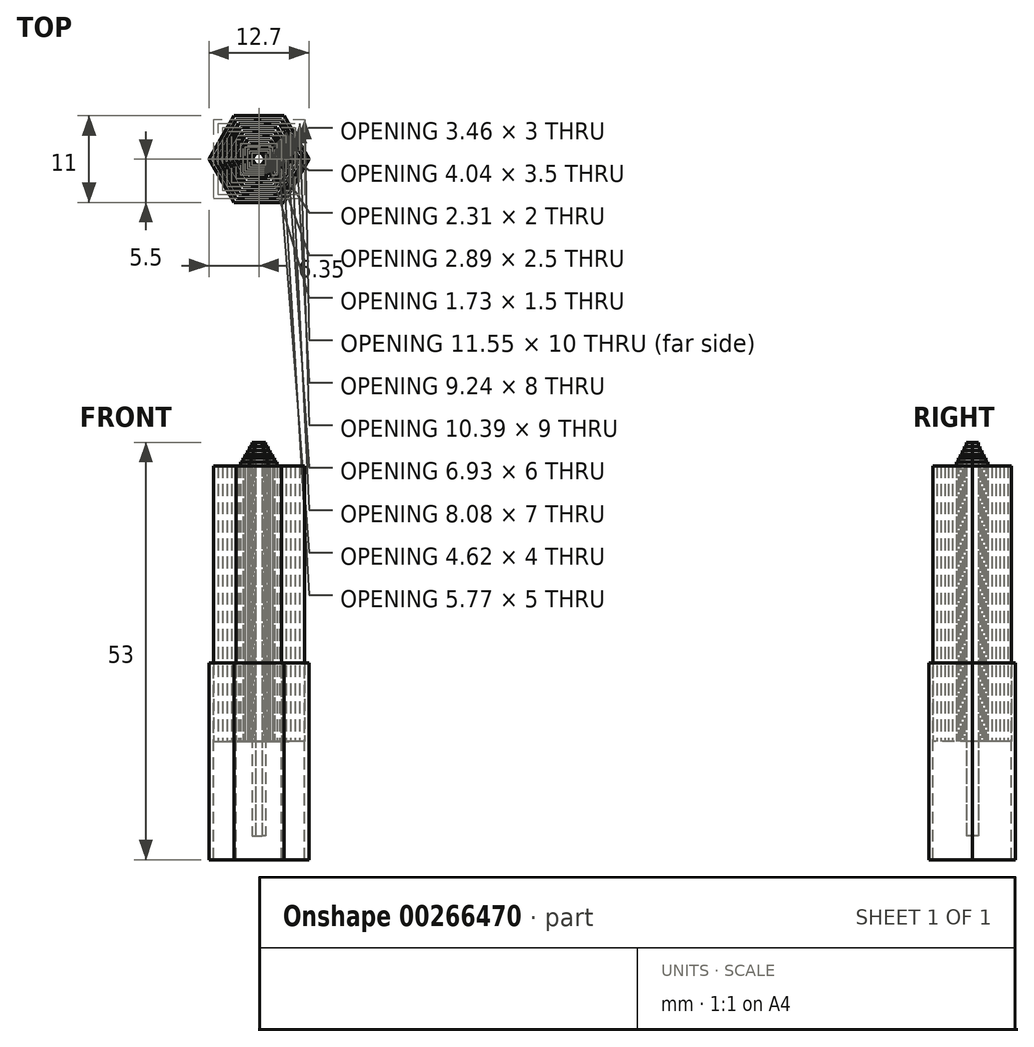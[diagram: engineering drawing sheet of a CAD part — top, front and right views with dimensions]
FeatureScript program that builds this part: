
annotation { "Feature Type Name" : "Feature", "Feature Type Description" : "" }
export const myFeature = defineFeature(function(context is Context, id is Id, definition is map)
    precondition{}
    {
        {
            var Q0;
            Q0=qCreatedBy(makeId("Top.planeOp"),FACE);
            var sketch = newSketch(context, id + "F0", { "sketchPlane" : qUnion([Q0])});
            skCircle(sketch, "E0.cCircle", {"center": v(0, 0) * mm, "radius": 0.87 * mm, "construction": true});
            skLineSegment(sketch, "E0.0", {"start": v(0.87, 0) * mm, "end": v(0.43, -0.75) * mm});
            skLineSegment(sketch, "E0.1", {"start": v(0.43, -0.75) * mm, "end": v(-0.43, -0.75) * mm});
            skLineSegment(sketch, "E0.2", {"start": v(-0.43, -0.75) * mm, "end": v(-0.87, 0) * mm});
            skLineSegment(sketch, "E0.3", {"start": v(-0.87, 0) * mm, "end": v(-0.43, 0.75) * mm});
            skLineSegment(sketch, "E0.4", {"start": v(-0.43, 0.75) * mm, "end": v(0.43, 0.75) * mm});
            skLineSegment(sketch, "E0.5", {"start": v(0.43, 0.75) * mm, "end": v(0.87, 0) * mm});
            skCircle(sketch, "E1.cCircle", {"center": v(0, 0) * mm, "radius": 1.15 * mm, "construction": true});
            skLineSegment(sketch, "E1.0", {"start": v(1.15, 0) * mm, "end": v(0.58, -1) * mm});
            skLineSegment(sketch, "E1.1", {"start": v(0.58, -1) * mm, "end": v(-0.58, -1) * mm});
            skLineSegment(sketch, "E1.2", {"start": v(-0.58, -1) * mm, "end": v(-1.15, 0) * mm});
            skLineSegment(sketch, "E1.3", {"start": v(-1.15, 0) * mm, "end": v(-0.58, 1) * mm});
            skLineSegment(sketch, "E1.4", {"start": v(-0.58, 1) * mm, "end": v(0.58, 1) * mm});
            skLineSegment(sketch, "E1.5", {"start": v(0.58, 1) * mm, "end": v(1.15, 0) * mm});
            skCircle(sketch, "E2.cCircle", {"center": v(0, 0) * mm, "radius": 1.44 * mm, "construction": true});
            skLineSegment(sketch, "E2.0", {"start": v(1.44, 0) * mm, "end": v(0.72, -1.25) * mm});
            skLineSegment(sketch, "E2.1", {"start": v(0.72, -1.25) * mm, "end": v(-0.72, -1.25) * mm});
            skLineSegment(sketch, "E2.2", {"start": v(-0.72, -1.25) * mm, "end": v(-1.44, 0) * mm});
            skLineSegment(sketch, "E2.3", {"start": v(-1.44, 0) * mm, "end": v(-0.72, 1.25) * mm});
            skLineSegment(sketch, "E2.4", {"start": v(-0.72, 1.25) * mm, "end": v(0.72, 1.25) * mm});
            skLineSegment(sketch, "E2.5", {"start": v(0.72, 1.25) * mm, "end": v(1.44, 0) * mm});
            skCircle(sketch, "E3.cCircle", {"center": v(0, 0) * mm, "radius": 1.73 * mm, "construction": true});
            skLineSegment(sketch, "E3.0", {"start": v(1.73, 0) * mm, "end": v(0.87, -1.5) * mm});
            skLineSegment(sketch, "E3.1", {"start": v(0.87, -1.5) * mm, "end": v(-0.87, -1.5) * mm});
            skLineSegment(sketch, "E3.2", {"start": v(-0.87, -1.5) * mm, "end": v(-1.73, 0) * mm});
            skLineSegment(sketch, "E3.3", {"start": v(-1.73, 0) * mm, "end": v(-0.87, 1.5) * mm});
            skLineSegment(sketch, "E3.4", {"start": v(-0.87, 1.5) * mm, "end": v(0.87, 1.5) * mm});
            skLineSegment(sketch, "E3.5", {"start": v(0.87, 1.5) * mm, "end": v(1.73, 0) * mm});
            skCircle(sketch, "E4.cCircle", {"center": v(0, 0) * mm, "radius": 2.02 * mm, "construction": true});
            skLineSegment(sketch, "E4.0", {"start": v(2.02, 0) * mm, "end": v(1.01, -1.75) * mm});
            skLineSegment(sketch, "E4.1", {"start": v(1.01, -1.75) * mm, "end": v(-1.01, -1.75) * mm});
            skLineSegment(sketch, "E4.2", {"start": v(-1.01, -1.75) * mm, "end": v(-2.02, 0) * mm});
            skLineSegment(sketch, "E4.3", {"start": v(-2.02, 0) * mm, "end": v(-1.01, 1.75) * mm});
            skLineSegment(sketch, "E4.4", {"start": v(-1.01, 1.75) * mm, "end": v(1.01, 1.75) * mm});
            skLineSegment(sketch, "E4.5", {"start": v(1.01, 1.75) * mm, "end": v(2.02, 0) * mm});
            skCircle(sketch, "E5.cCircle", {"center": v(0, 0) * mm, "radius": 2.3 * mm, "construction": true});
            skLineSegment(sketch, "E5.0", {"start": v(2.3, 0) * mm, "end": v(1.15, -2) * mm});
            skLineSegment(sketch, "E5.1", {"start": v(1.15, -2) * mm, "end": v(-1.15, -2) * mm});
            skLineSegment(sketch, "E5.2", {"start": v(-1.15, -2) * mm, "end": v(-2.3, 0) * mm});
            skLineSegment(sketch, "E5.3", {"start": v(-2.3, 0) * mm, "end": v(-1.15, 2) * mm});
            skLineSegment(sketch, "E5.4", {"start": v(-1.15, 2) * mm, "end": v(1.15, 2) * mm});
            skLineSegment(sketch, "E5.5", {"start": v(1.15, 2) * mm, "end": v(2.3, 0) * mm});
            skCircle(sketch, "E6.cCircle", {"center": v(0, 0) * mm, "radius": 4.04 * mm, "construction": true});
            skLineSegment(sketch, "E6.0", {"start": v(4.04, 0) * mm, "end": v(2.02, -3.5) * mm});
            skLineSegment(sketch, "E6.1", {"start": v(2.02, -3.5) * mm, "end": v(-2.02, -3.5) * mm});
            skLineSegment(sketch, "E6.2", {"start": v(-2.02, -3.5) * mm, "end": v(-4.04, 0) * mm});
            skLineSegment(sketch, "E6.3", {"start": v(-4.04, 0) * mm, "end": v(-2.02, 3.5) * mm});
            skLineSegment(sketch, "E6.4", {"start": v(-2.02, 3.5) * mm, "end": v(2.02, 3.5) * mm});
            skLineSegment(sketch, "E6.5", {"start": v(2.02, 3.5) * mm, "end": v(4.04, 0) * mm});
            skCircle(sketch, "E7.cCircle", {"center": v(0, 0) * mm, "radius": 4.62 * mm, "construction": true});
            skLineSegment(sketch, "E7.0", {"start": v(4.62, 0) * mm, "end": v(2.3, -4) * mm});
            skLineSegment(sketch, "E7.1", {"start": v(2.3, -4) * mm, "end": v(-2.3, -4) * mm});
            skLineSegment(sketch, "E7.2", {"start": v(-2.3, -4) * mm, "end": v(-4.62, 0) * mm});
            skLineSegment(sketch, "E7.3", {"start": v(-4.62, 0) * mm, "end": v(-2.3, 4) * mm});
            skLineSegment(sketch, "E7.4", {"start": v(-2.3, 4) * mm, "end": v(2.3, 4) * mm});
            skLineSegment(sketch, "E7.5", {"start": v(2.3, 4) * mm, "end": v(4.62, 0) * mm});
            skCircle(sketch, "E8.cCircle", {"center": v(0, 0) * mm, "radius": 5.2 * mm, "construction": true});
            skLineSegment(sketch, "E8.0", {"start": v(5.2, 0) * mm, "end": v(2.6, -4.5) * mm});
            skLineSegment(sketch, "E8.1", {"start": v(2.6, -4.5) * mm, "end": v(-2.6, -4.5) * mm});
            skLineSegment(sketch, "E8.2", {"start": v(-2.6, -4.5) * mm, "end": v(-5.2, 0) * mm});
            skLineSegment(sketch, "E8.3", {"start": v(-5.2, 0) * mm, "end": v(-2.6, 4.5) * mm});
            skLineSegment(sketch, "E8.4", {"start": v(-2.6, 4.5) * mm, "end": v(2.6, 4.5) * mm});
            skLineSegment(sketch, "E8.5", {"start": v(2.6, 4.5) * mm, "end": v(5.2, 0) * mm});
            skCircle(sketch, "E9.cCircle", {"center": v(0, 0) * mm, "radius": 5.77 * mm, "construction": true});
            skLineSegment(sketch, "E9.0", {"start": v(5.77, 0) * mm, "end": v(2.89, -5) * mm});
            skLineSegment(sketch, "E9.1", {"start": v(2.89, -5) * mm, "end": v(-2.89, -5) * mm});
            skLineSegment(sketch, "E9.2", {"start": v(-2.89, -5) * mm, "end": v(-5.77, 0) * mm});
            skLineSegment(sketch, "E9.3", {"start": v(-5.77, 0) * mm, "end": v(-2.89, 5) * mm});
            skLineSegment(sketch, "E9.4", {"start": v(-2.89, 5) * mm, "end": v(2.89, 5) * mm});
            skLineSegment(sketch, "E9.5", {"start": v(2.89, 5) * mm, "end": v(5.77, 0) * mm});
            skCircle(sketch, "E10.cCircle", {"center": v(0, 0) * mm, "radius": 2.89 * mm, "construction": true});
            skLineSegment(sketch, "E10.0", {"start": v(2.89, 0) * mm, "end": v(1.44, -2.5) * mm});
            skLineSegment(sketch, "E10.1", {"start": v(1.44, -2.5) * mm, "end": v(-1.44, -2.5) * mm});
            skLineSegment(sketch, "E10.2", {"start": v(-1.44, -2.5) * mm, "end": v(-2.89, 0) * mm});
            skLineSegment(sketch, "E10.3", {"start": v(-2.89, 0) * mm, "end": v(-1.44, 2.5) * mm});
            skLineSegment(sketch, "E10.4", {"start": v(-1.44, 2.5) * mm, "end": v(1.44, 2.5) * mm});
            skLineSegment(sketch, "E10.5", {"start": v(1.44, 2.5) * mm, "end": v(2.89, 0) * mm});
            skCircle(sketch, "E11.cCircle", {"center": v(0, 0) * mm, "radius": 3.46 * mm, "construction": true});
            skLineSegment(sketch, "E11.0", {"start": v(3.46, 0) * mm, "end": v(1.73, -3) * mm});
            skLineSegment(sketch, "E11.1", {"start": v(1.73, -3) * mm, "end": v(-1.73, -3) * mm});
            skLineSegment(sketch, "E11.2", {"start": v(-1.73, -3) * mm, "end": v(-3.46, 0) * mm});
            skLineSegment(sketch, "E11.3", {"start": v(-3.46, 0) * mm, "end": v(-1.73, 3) * mm});
            skLineSegment(sketch, "E11.4", {"start": v(-1.73, 3) * mm, "end": v(1.73, 3) * mm});
            skLineSegment(sketch, "E11.5", {"start": v(1.73, 3) * mm, "end": v(3.46, 0) * mm});
            skCircle(sketch, "E12.cCircle", {"center": v(0, 0) * mm, "radius": 6.35 * mm, "construction": true});
            skLineSegment(sketch, "E12.0", {"start": v(6.35, 0) * mm, "end": v(3.18, -5.5) * mm});
            skLineSegment(sketch, "E12.1", {"start": v(3.18, -5.5) * mm, "end": v(-3.18, -5.5) * mm});
            skLineSegment(sketch, "E12.2", {"start": v(-3.18, -5.5) * mm, "end": v(-6.35, 0) * mm});
            skLineSegment(sketch, "E12.3", {"start": v(-6.35, 0) * mm, "end": v(-3.18, 5.5) * mm});
            skLineSegment(sketch, "E12.4", {"start": v(-3.18, 5.5) * mm, "end": v(3.18, 5.5) * mm});
            skLineSegment(sketch, "E12.5", {"start": v(3.18, 5.5) * mm, "end": v(6.35, 0) * mm});
            skSolve(sketch);
        }
        {
            var Q0;
            Q0=makeQuery(id+"F0.imprint","IMPRINT",FACE,{"disambiguationData":[TD([[makeQuery(id+"F0.imprint","IMPRINT",EDGE,{"derivedFrom":sQuery(id+"F0.wireOp",EDGE,"E9.0")}),1.0]])]});
            extrude(context, id + "F1", {"entities" : qUnion([Q0]), "oppositeDirection" : true, "depth" : 25 * mm});
        }
        {
            var Q0;
            Q0=makeQuery(id+"F0.imprint","IMPRINT",FACE,{"disambiguationData":[TD([[makeQuery(id+"F0.imprint","IMPRINT",EDGE,{"derivedFrom":sQuery(id+"F0.wireOp",EDGE,"E0.0")}),-1.0]])]});
            extrude(context, id + "F2", {"entities" : qUnion([Q0]), "depth" : 28 * mm, "hasSecondDirection" : true, "secondDirectionOppositeDirection" : true, "secondDirectionDepth" : 22 * mm});
        }
        {
            var Q0;
            Q0=makeQuery(id+"F0.imprint","IMPRINT",FACE,{"disambiguationData":[TD([[makeQuery(id+"F0.imprint","IMPRINT",EDGE,{"derivedFrom":sQuery(id+"F0.wireOp",EDGE,"E0.0")}),1.0]])]});
            extrude(context, id + "F3", {"entities" : qUnion([Q0]), "depth" : 27.5 * mm, "hasSecondDirection" : true, "secondDirectionOppositeDirection" : true, "secondDirectionDepth" : 10 * mm});
        }
        {
            var Q0;
            Q0=makeQuery(id+"F0.imprint","IMPRINT",FACE,{"disambiguationData":[TD([[makeQuery(id+"F0.imprint","IMPRINT",EDGE,{"derivedFrom":sQuery(id+"F0.wireOp",EDGE,"E1.0")}),1.0]])]});
            extrude(context, id + "F4", {"entities" : qUnion([Q0]), "depth" : 27 * mm, "hasSecondDirection" : true, "secondDirectionOppositeDirection" : true, "secondDirectionDepth" : 10 * mm});
        }
        {
            var Q0;
            Q0=makeQuery(id+"F0.imprint","IMPRINT",FACE,{"disambiguationData":[TD([[makeQuery(id+"F0.imprint","IMPRINT",EDGE,{"derivedFrom":sQuery(id+"F0.wireOp",EDGE,"E2.0")}),1.0]])]});
            extrude(context, id + "F5", {"entities" : qUnion([Q0]), "depth" : 26.5 * mm, "hasSecondDirection" : true, "secondDirectionOppositeDirection" : true, "secondDirectionDepth" : 10 * mm});
        }
        {
            var Q0;
            Q0=makeQuery(id+"F0.imprint","IMPRINT",FACE,{"disambiguationData":[TD([[makeQuery(id+"F0.imprint","IMPRINT",EDGE,{"derivedFrom":sQuery(id+"F0.wireOp",EDGE,"E3.0")}),1.0]])]});
            extrude(context, id + "F6", {"entities" : qUnion([Q0]), "depth" : 26 * mm, "hasSecondDirection" : true, "secondDirectionOppositeDirection" : true, "secondDirectionDepth" : 10 * mm});
        }
        {
            var Q0;
            Q0=makeQuery(id+"F0.imprint","IMPRINT",FACE,{"disambiguationData":[TD([[makeQuery(id+"F0.imprint","IMPRINT",EDGE,{"derivedFrom":sQuery(id+"F0.wireOp",EDGE,"E4.0")}),1.0]])]});
            extrude(context, id + "F7", {"entities" : qUnion([Q0]), "depth" : 25.5 * mm, "hasSecondDirection" : true, "secondDirectionOppositeDirection" : true, "secondDirectionDepth" : 10 * mm});
        }
        {
            var Q0;
            Q0=makeQuery(id+"F0.imprint","IMPRINT",FACE,{"disambiguationData":[TD([[makeQuery(id+"F0.imprint","IMPRINT",EDGE,{"derivedFrom":sQuery(id+"F0.wireOp",EDGE,"E5.0")}),1.0]])]});
            extrude(context, id + "F8", {"entities" : qUnion([Q0]), "depth" : 25 * mm, "hasSecondDirection" : true, "secondDirectionOppositeDirection" : true, "secondDirectionDepth" : 10 * mm});
        }
        {
            var Q0;
            Q0=makeQuery(id+"F0.imprint","IMPRINT",FACE,{"disambiguationData":[TD([[makeQuery(id+"F0.imprint","IMPRINT",EDGE,{"derivedFrom":sQuery(id+"F0.wireOp",EDGE,"E10.0")}),1.0]])]});
            extrude(context, id + "F9", {"entities" : qUnion([Q0]), "depth" : 25 * mm, "hasSecondDirection" : true, "secondDirectionOppositeDirection" : true, "secondDirectionDepth" : 10 * mm});
        }
        {
            var Q0;
            Q0=makeQuery(id+"F0.imprint","IMPRINT",FACE,{"disambiguationData":[TD([[makeQuery(id+"F0.imprint","IMPRINT",EDGE,{"derivedFrom":sQuery(id+"F0.wireOp",EDGE,"E6.0")}),-1.0]])]});
            extrude(context, id + "F10", {"entities" : qUnion([Q0]), "depth" : 25 * mm, "hasSecondDirection" : true, "secondDirectionOppositeDirection" : true, "secondDirectionDepth" : 10 * mm});
        }
        {
            var Q0;
            Q0=makeQuery(id+"F0.imprint","IMPRINT",FACE,{"disambiguationData":[TD([[makeQuery(id+"F0.imprint","IMPRINT",EDGE,{"derivedFrom":sQuery(id+"F0.wireOp",EDGE,"E6.0")}),1.0]])]});
            extrude(context, id + "F11", {"entities" : qUnion([Q0]), "depth" : 25 * mm, "hasSecondDirection" : true, "secondDirectionOppositeDirection" : true, "secondDirectionDepth" : 10 * mm});
        }
        {
            var Q0;
            Q0=makeQuery(id+"F0.imprint","IMPRINT",FACE,{"disambiguationData":[TD([[makeQuery(id+"F0.imprint","IMPRINT",EDGE,{"derivedFrom":sQuery(id+"F0.wireOp",EDGE,"E7.0")}),1.0]])]});
            extrude(context, id + "F12", {"entities" : qUnion([Q0]), "depth" : 25 * mm, "hasSecondDirection" : true, "secondDirectionOppositeDirection" : true, "secondDirectionDepth" : 10 * mm});
        }
        {
            var Q0;
            Q0=makeQuery(id+"F0.imprint","IMPRINT",FACE,{"disambiguationData":[TD([[makeQuery(id+"F0.imprint","IMPRINT",EDGE,{"derivedFrom":sQuery(id+"F0.wireOp",EDGE,"E8.0")}),1.0]])]});
            extrude(context, id + "F13", {"entities" : qUnion([Q0]), "depth" : 25 * mm, "hasSecondDirection" : true, "secondDirectionOppositeDirection" : true, "secondDirectionDepth" : 10 * mm});
        }
    });
